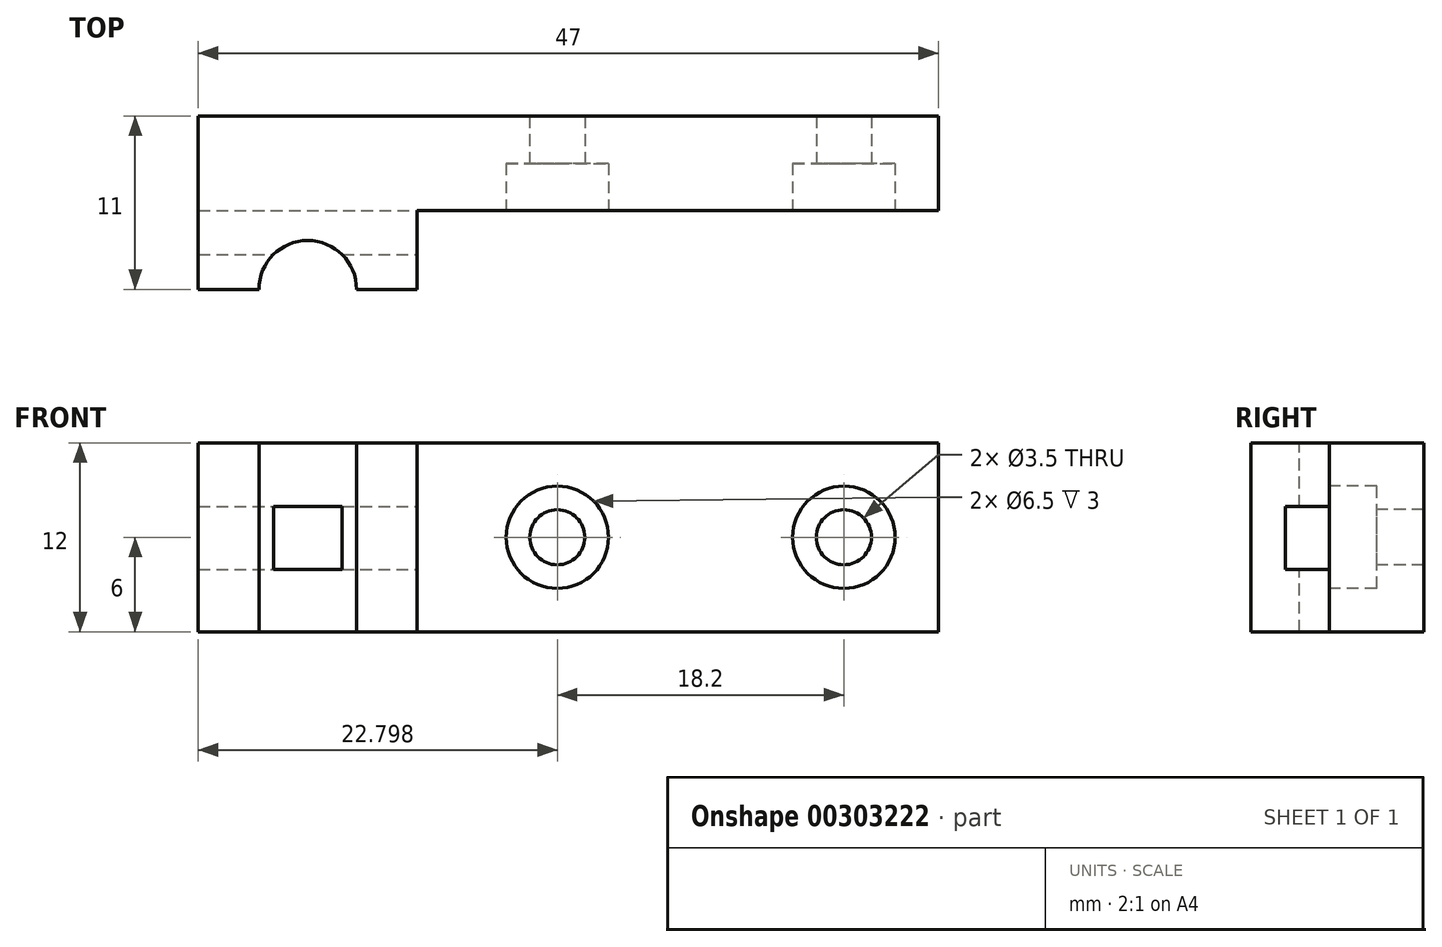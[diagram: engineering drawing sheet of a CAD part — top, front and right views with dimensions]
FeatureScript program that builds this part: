
annotation { "Feature Type Name" : "Feature", "Feature Type Description" : "" }
export const myFeature = defineFeature(function(context is Context, id is Id, definition is map)
    precondition{}
    {
        {
            var Q0;
            Q0=qCreatedBy(makeId("Top.planeOp"),FACE);
            var sketch = newSketch(context, id + "F0", { "sketchPlane" : qUnion([Q0])});
            skLineSegment(sketch, "E0", {"start": v(19.8, 0) * mm, "end": v(19.8, 6) * mm});
            skLineSegment(sketch, "E1", {"start": v(19.8, 6) * mm, "end": v(-27.2, 6) * mm});
            skLineSegment(sketch, "E2", {"start": v(-27.2, 6) * mm, "end": v(-27.2, -5) * mm});
            skLineSegment(sketch, "E3", {"start": v(-27.2, -5) * mm, "end": v(-13.29, -5) * mm});
            skLineSegment(sketch, "E4", {"start": v(-13.29, -5) * mm, "end": v(-13.29, 0) * mm});
            skLineSegment(sketch, "E5", {"start": v(-13.29, 0) * mm, "end": v(19.8, 0) * mm});
            skSolve(sketch);
        }
        {
            var Q0;
            Q0 = qSketchRegion(id + "F0", true);
            extrude(context, id + "F1", {"entities" : qUnion([Q0]), "depth" : 12 * mm});
        }
        {
            var Q0;
            Q0=makeQuery(id+"F1.opExtrude","CAP_FACE",FACE,{"disambiguationData":[OSD([sQuery(id+"F0.wireOp",EDGE,"E0"),sQuery(id+"F0.wireOp",EDGE,"E1"),sQuery(id+"F0.wireOp",EDGE,"E2"),sQuery(id+"F0.wireOp",EDGE,"E3"),sQuery(id+"F0.wireOp",EDGE,"E4"),sQuery(id+"F0.wireOp",EDGE,"E5")])],"isStart":false});
            var sketch = newSketch(context, id + "F2", { "sketchPlane" : qUnion([Q0])});
            skCircle(sketch, "E6", {"center": v(-20.24, -5) * mm, "radius": 3.1 * mm});
            skSolve(sketch);
        }
        {
            var Q0;
            Q0 = qSketchRegion(id + "F2", true);
            extrude(context, id + "F3", {"entities" : qUnion([Q0]), "operationType" : NewBodyOperationType.REMOVE, "endBound" : BoundingType.THROUGH_ALL, "oppositeDirection" : true, "depth" : 25 * mm});
        }
        {
            var Q0;
            Q0=makeQuery(id+"F1.opExtrude","SWEPT_FACE",FACE,{"disambiguationData":[OSD([sQuery(id+"F0.wireOp",EDGE,"E5")])]});
            var sketch = newSketch(context, id + "F4", { "sketchPlane" : qUnion([Q0])});
            skCircle(sketch, "E7", {"center": v(13.8, 6) * mm, "radius": 1.75 * mm});
            skPoint(sketch, "E7.centerSnap0", {"position": v(19.8, 6) * mm});
            skCircle(sketch, "E8", {"center": v(-4.4, 6) * mm, "radius": 1.75 * mm});
            skLineSegment(sketch, "E9", {"start": v(-20.4, 18.92) * mm, "end": v(-20.4, -6.08) * mm, "construction": true});
            skSolve(sketch);
        }
        {
            var Q0;
            Q0 = qSketchRegion(id + "F4", true);
            extrude(context, id + "F5", {"entities" : qUnion([Q0]), "operationType" : NewBodyOperationType.REMOVE, "endBound" : BoundingType.THROUGH_ALL, "oppositeDirection" : true, "depth" : 25 * mm});
        }
        {
            var Q0;
            Q0=makeQuery(id+"F1.opExtrude","SWEPT_FACE",FACE,{"disambiguationData":[OSD([sQuery(id+"F0.wireOp",EDGE,"E5")])]});
            var sketch = newSketch(context, id + "F6", { "sketchPlane" : qUnion([Q0])});
            skCircle(sketch, "E10", {"center": v(-4.4, 6) * mm, "radius": 3.25 * mm});
            skCircle(sketch, "E11", {"center": v(13.8, 6) * mm, "radius": 3.25 * mm});
            skSolve(sketch);
        }
        {
            var Q0;
            Q0 = qSketchRegion(id + "F6", true);
            extrude(context, id + "F7", {"entities" : qUnion([Q0]), "operationType" : NewBodyOperationType.REMOVE, "oppositeDirection" : true, "depth" : 3 * mm});
        }
        {
            var Q0;
            Q0=makeQuery(id+"F1.opExtrude","SWEPT_FACE",FACE,{"disambiguationData":[OSD([sQuery(id+"F0.wireOp",EDGE,"E4")])]});
            var sketch = newSketch(context, id + "F8", { "sketchPlane" : qUnion([Q0])});
            skLineSegment(sketch, "E12.bottom", {"start": v(0, 3.95) * mm, "end": v(-2.8, 3.95) * mm});
            skLineSegment(sketch, "E12.top", {"start": v(0, 7.95) * mm, "end": v(-2.8, 7.95) * mm});
            skLineSegment(sketch, "E12.left", {"start": v(0, 3.95) * mm, "end": v(0, 7.95) * mm});
            skLineSegment(sketch, "E12.right", {"start": v(-2.8, 3.95) * mm, "end": v(-2.8, 7.95) * mm});
            skSolve(sketch);
        }
        {
            var Q0;
            Q0 = qSketchRegion(id + "F8", true);
            extrude(context, id + "F9", {"entities" : qUnion([Q0]), "operationType" : NewBodyOperationType.REMOVE, "endBound" : BoundingType.THROUGH_ALL, "oppositeDirection" : true, "depth" : 25 * mm});
        }
    });
